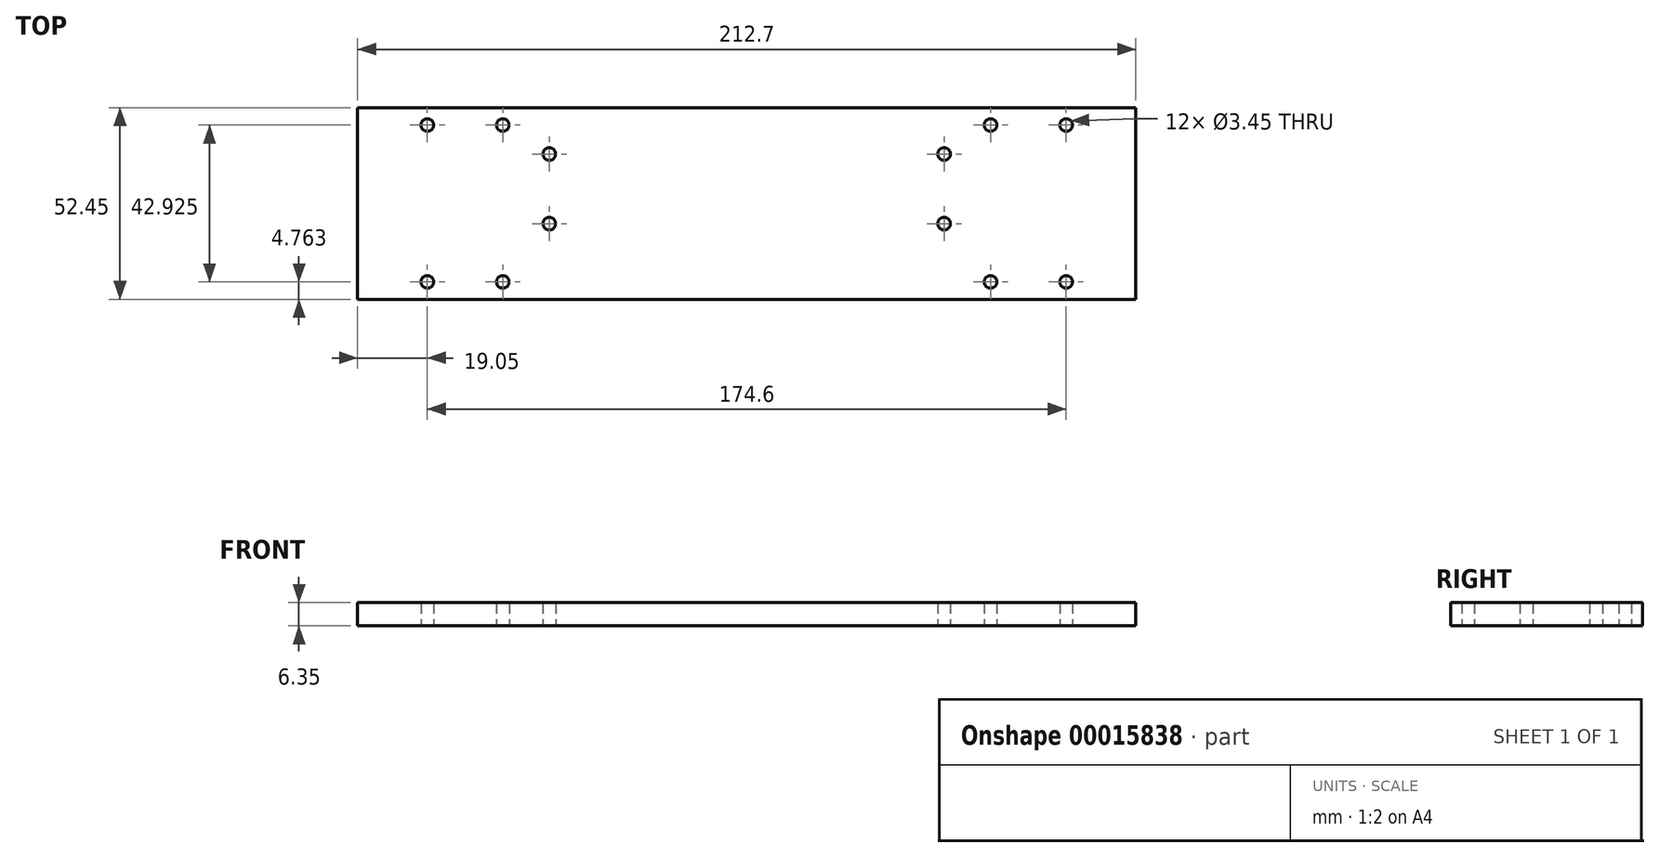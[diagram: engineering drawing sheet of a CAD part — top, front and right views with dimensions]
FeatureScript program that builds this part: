
annotation { "Feature Type Name" : "Feature", "Feature Type Description" : "" }
export const myFeature = defineFeature(function(context is Context, id is Id, definition is map)
    precondition{}
    {
        {
            var Q0;
            Q0=qCreatedBy(makeId("Top.planeOp"),FACE);
            var sketch = newSketch(context, id + "F0", { "sketchPlane" : qUnion([Q0])});
            skLineSegment(sketch, "E0.bottom", {"start": v(0, 0) * mm, "end": v(-212.7, 0) * mm});
            skLineSegment(sketch, "E0.top", {"start": v(0, -52.45) * mm, "end": v(-212.7, -52.45) * mm});
            skLineSegment(sketch, "E0.left", {"start": v(0, 0) * mm, "end": v(0, -52.45) * mm});
            skLineSegment(sketch, "E0.right", {"start": v(-212.7, 0) * mm, "end": v(-212.7, -52.45) * mm});
            skLineSegment(sketch, "E1", {"start": v(0, -47.69) * mm, "end": v(-19.05, -47.69) * mm});
            skLineSegment(sketch, "E2", {"start": v(-19.05, -47.69) * mm, "end": v(-39.69, -47.69) * mm, "construction": true});
            skLineSegment(sketch, "E3", {"start": v(0, -4.76) * mm, "end": v(-19.05, -4.76) * mm});
            skLineSegment(sketch, "E4", {"start": v(-19.05, -4.76) * mm, "end": v(-39.69, -4.76) * mm, "construction": true});
            skLineSegment(sketch, "E5", {"start": v(-212.7, -4.76) * mm, "end": v(-193.65, -4.76) * mm});
            skLineSegment(sketch, "E6", {"start": v(-193.65, -4.76) * mm, "end": v(-173.01, -4.76) * mm, "construction": true});
            skLineSegment(sketch, "E7", {"start": v(-212.7, -47.69) * mm, "end": v(-193.65, -47.69) * mm});
            skLineSegment(sketch, "E8", {"start": v(-193.65, -47.69) * mm, "end": v(-173.01, -47.69) * mm, "construction": true});
            skLineSegment(sketch, "E9", {"start": v(-19.05, -4.76) * mm, "end": v(-19.05, 0) * mm, "construction": true});
            skLineSegment(sketch, "E10", {"start": v(-19.05, -47.69) * mm, "end": v(-19.05, -52.45) * mm, "construction": true});
            skCircle(sketch, "E11", {"center": v(-19.05, -47.69) * mm, "radius": 1.73 * mm});
            skCircle(sketch, "E12", {"center": v(-19.05, -4.76) * mm, "radius": 1.73 * mm});
            skCircle(sketch, "E13", {"center": v(-173.01, -4.76) * mm, "radius": 1.73 * mm});
            skCircle(sketch, "E14", {"center": v(-39.69, -4.76) * mm, "radius": 1.73 * mm});
            skCircle(sketch, "E15", {"center": v(-39.69, -47.69) * mm, "radius": 1.73 * mm});
            skCircle(sketch, "E16", {"center": v(-173.01, -47.69) * mm, "radius": 1.73 * mm});
            skCircle(sketch, "E17", {"center": v(-193.65, -47.69) * mm, "radius": 1.73 * mm});
            skCircle(sketch, "E18", {"center": v(-193.65, -4.76) * mm, "radius": 1.73 * mm});
            skLineSegment(sketch, "E19", {"start": v(-173.01, -4.76) * mm, "end": v(-160.31, -4.76) * mm});
            skLineSegment(sketch, "E20", {"start": v(-160.31, 0) * mm, "end": v(-160.31, -12.7) * mm});
            skLineSegment(sketch, "E21", {"start": v(-160.31, -12.7) * mm, "end": v(-160.31, -31.75) * mm});
            skLineSegment(sketch, "E22", {"start": v(-52.39, 0) * mm, "end": v(-52.39, -12.7) * mm});
            skLineSegment(sketch, "E23", {"start": v(-52.39, -12.7) * mm, "end": v(-52.39, -31.75) * mm});
            skLineSegment(sketch, "E24", {"start": v(-39.69, -4.76) * mm, "end": v(-52.39, -4.76) * mm});
            skCircle(sketch, "E25", {"center": v(-160.31, -12.7) * mm, "radius": 1.73 * mm});
            skCircle(sketch, "E26", {"center": v(-160.31, -31.75) * mm, "radius": 1.73 * mm});
            skCircle(sketch, "E27", {"center": v(-52.39, -31.75) * mm, "radius": 1.73 * mm});
            skCircle(sketch, "E28", {"center": v(-52.39, -12.7) * mm, "radius": 1.73 * mm});
            skSolve(sketch);
        }
        {
            var Q0;
            Q0 = qSketchRegion(id + "F0", true);
            extrude(context, id + "F1", {"entities" : qUnion([Q0]), "depth" : 6.35 * mm});
        }
    });
